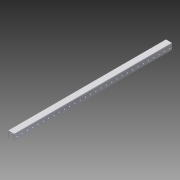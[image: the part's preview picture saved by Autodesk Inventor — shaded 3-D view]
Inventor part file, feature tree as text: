
AUTODESK INVENTOR PART (.ipt)
format: ipt  version: 2015 (Build 190159000, 159)  size: 262,656 bytes
history: native  units: in
note: dims shown in document units (in); Inventor stores cm internally (conversion verified against a paired STEP export)
features: extrude x2, sketch x2, pattern_linear x1
ambient origin geometry x8: Origin, YZ Plane, XZ Plane, XY Plane, X Axis, Y Axis, Z Axis, Center Point
bodies: Solid1 (feature_tree)
feature tree (5):
  extrude  "Extrusion1"  Depth=30.0in
  extrude  "Extrusion4"  Depth=0.5in
  pattern_linear  "Rectangular Pattern3"  Spacing1=0.5in  [1 undecoded]
  sketch  "Sketch1"  dims[d0=1.13in d1=1.25in d2=0.125in d3=0.125in d4=0.125in d5=30.0in]
  sketch  "Sketch4"  dims[d6=0.0in d35=0.5in d36=0.5in d37=0.25in d38=1.0in d39=0.0in d40=7.874in d42=1.0in d43=7.874in d45=1.0in]
note: 1 required parameter value undecoded (feature->parameter linkage not recoverable at this tier; creation-order binding heuristic only, values carry confidence <= 0.55)
